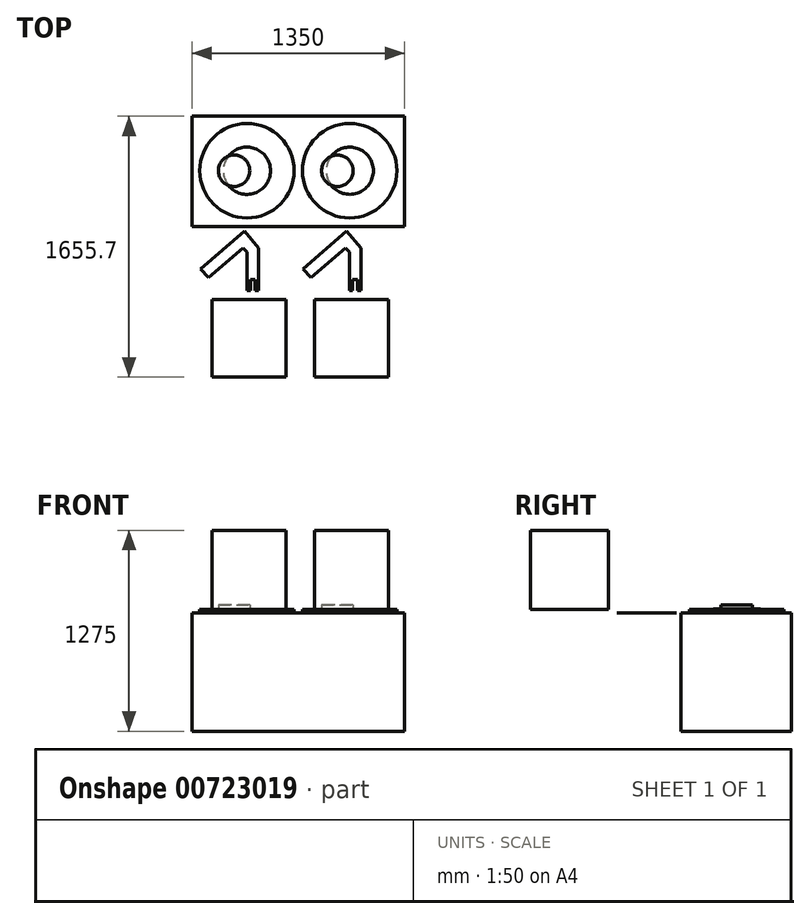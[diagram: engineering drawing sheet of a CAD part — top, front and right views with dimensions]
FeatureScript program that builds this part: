
annotation { "Feature Type Name" : "Feature", "Feature Type Description" : "" }
export const myFeature = defineFeature(function(context is Context, id is Id, definition is map)
    precondition{}
    {
        {
            var Q0;
            Q0=qCreatedBy(makeId("Top.planeOp"),FACE);
            var sketch = newSketch(context, id + "F0", { "sketchPlane" : qUnion([Q0])});
            skLineSegment(sketch, "E0.bottom", {"start": v(-348.1, 345.76) * mm, "end": v(1001.9, 345.76) * mm});
            skLineSegment(sketch, "E0.top", {"start": v(-348.1, -354.24) * mm, "end": v(1001.9, -354.24) * mm});
            skLineSegment(sketch, "E0.left", {"start": v(-348.1, 345.76) * mm, "end": v(-348.1, -354.24) * mm});
            skLineSegment(sketch, "E0.right", {"start": v(1001.9, 345.76) * mm, "end": v(1001.9, -354.24) * mm});
            skSolve(sketch);
        }
        {
            var Q0;
            Q0=makeQuery(id+"F0.imprint","IMPRINT",FACE,{"disambiguationData":[TD([[makeQuery(id+"F0.imprint","IMPRINT",EDGE,{"derivedFrom":sQuery(id+"F0.wireOp",EDGE,"E0.bottom")}),-1.0]])]});
            extrude(context, id + "F1", {"entities" : qUnion([Q0]), "depth" : 750 * mm, "offsetDistance" : 25 * mm});
        }
        {
            var Q0;
            Q0=makeQuery(id+"F1.opExtrude","CAP_FACE",FACE,{"disambiguationData":[OSD([sQuery(id+"F0.wireOp",EDGE,"E0.bottom"),sQuery(id+"F0.wireOp",EDGE,"E0.top"),sQuery(id+"F0.wireOp",EDGE,"E0.left"),sQuery(id+"F0.wireOp",EDGE,"E0.right")])],"isStart":false});
            var sketch = newSketch(context, id + "F2", { "sketchPlane" : qUnion([Q0])});
            skCircle(sketch, "E1", {"center": v(0, 0) * mm, "radius": 300 * mm});
            skCircle(sketch, "E2", {"center": v(652.85, 0) * mm, "radius": 300 * mm});
            skSolve(sketch);
        }
        {
            var Q0;
            Q0=makeQuery(id+"F2.imprint","IMPRINT",FACE,{"disambiguationData":[TD([[makeQuery(id+"F2.imprint","IMPRINT",EDGE,{"derivedFrom":sQuery(id+"F2.wireOp",EDGE,"E1")}),1.0]])]});
            var Q1;
            Q1=makeQuery(id+"F2.imprint","IMPRINT",FACE,{"disambiguationData":[TD([[makeQuery(id+"F2.imprint","IMPRINT",EDGE,{"derivedFrom":sQuery(id+"F2.wireOp",EDGE,"E2")}),1.0]])]});
            extrude(context, id + "F3", {"entities" : qUnion([Q0, Q1]), "operationType" : NewBodyOperationType.ADD, "depth" : 25 * mm, "offsetDistance" : 25 * mm});
        }
        {
            var Q0;
            Q0=makeQuery(id+"F3.opExtrude","CAP_FACE",FACE,{"disambiguationData":[OSD([sQuery(id+"F2.wireOp",EDGE,"E1")])],"isStart":false});
            var sketch = newSketch(context, id + "F4", { "sketchPlane" : qUnion([Q0])});
            skCircle(sketch, "E3", {"center": v(0, 0) * mm, "radius": 150 * mm});
            skCircle(sketch, "E4", {"center": v(652.98, 0) * mm, "radius": 150 * mm});
            skSolve(sketch);
        }
        {
            var Q0;
            Q0=makeQuery(id+"F4.imprint","IMPRINT",FACE,{"disambiguationData":[TD([[makeQuery(id+"F4.imprint","IMPRINT",EDGE,{"derivedFrom":sQuery(id+"F4.wireOp",EDGE,"E3")}),1.0]])]});
            var Q1;
            Q1=makeQuery(id+"F4.imprint","IMPRINT",FACE,{"disambiguationData":[TD([[makeQuery(id+"F4.imprint","IMPRINT",EDGE,{"derivedFrom":sQuery(id+"F4.wireOp",EDGE,"E4")}),1.0]])]});
            extrude(context, id + "F5", {"entities" : qUnion([Q0, Q1]), "operationType" : NewBodyOperationType.ADD, "depth" : 2 * mm, "offsetDistance" : 25 * mm});
        }
        {
            var Q0;
            Q0=makeQuery(id+"F5.opExtrude","CAP_FACE",FACE,{"disambiguationData":[OSD([sQuery(id+"F4.wireOp",EDGE,"E3")])],"isStart":false});
            var sketch = newSketch(context, id + "F6", { "sketchPlane" : qUnion([Q0])});
            skCircle(sketch, "E5", {"center": v(-81.59, 0) * mm, "radius": 100 * mm});
            skCircle(sketch, "E6", {"center": v(574.27, 0) * mm, "radius": 100 * mm});
            skSolve(sketch);
        }
        {
            var Q0;
            {var subQ0=sQuery(id+"F6.wireOp",EDGE,"E5");var subQ1=makeQuery(id+"F5.opExtrude","CAP_EDGE",EDGE,{"disambiguationData":[OSD([sQuery(id+"F4.wireOp",EDGE,"E3")])],"isStart":false});var subQ2=makeQuery(id+"F6.imprint","INTERSECT",VERTEX,{"disambiguationData":[OD(0.0)],"derivedFrom":[subQ1,subQ0]});Q0=makeQuery(id+"F6.imprint","IMPRINT",FACE,{"disambiguationData":[TD([[makeQuery(id+"F6.imprint","IMPRINT",EDGE,{"disambiguationData":[TD([[subQ2,1.0]])],"derivedFrom":subQ0}),1.0]])]});}
            var Q1;
            {var subQ0=sQuery(id+"F6.wireOp",EDGE,"E5");var subQ1=makeQuery(id+"F5.opExtrude","CAP_EDGE",EDGE,{"disambiguationData":[OSD([sQuery(id+"F4.wireOp",EDGE,"E3")])],"isStart":false});var subQ2=makeQuery(id+"F6.imprint","INTERSECT",VERTEX,{"disambiguationData":[OD(0.0)],"derivedFrom":[subQ1,subQ0]});Q1=makeQuery(id+"F6.imprint","IMPRINT",FACE,{"disambiguationData":[TD([[makeQuery(id+"F6.imprint","IMPRINT",EDGE,{"disambiguationData":[TD([[subQ2,-1.0]])],"derivedFrom":subQ0}),1.0]])]});}
            var Q2;
            Q2=makeQuery(id+"F6.imprint","IMPRINT",FACE,{"disambiguationData":[TD([[makeQuery(id+"F6.imprint","IMPRINT",EDGE,{"derivedFrom":sQuery(id+"F6.wireOp",EDGE,"E6")}),1.0]])]});
            extrude(context, id + "F7", {"entities" : qUnion([Q0, Q1, Q2]), "operationType" : NewBodyOperationType.ADD, "depth" : 25 * mm, "offsetDistance" : 25 * mm});
        }
        {
            var Q0;
            Q0=makeQuery(id+"F1.opExtrude","SWEPT_BODY",BODY,{"disambiguationData":[OSD([sQuery(id+"F0.wireOp",EDGE,"E0.bottom"),sQuery(id+"F0.wireOp",EDGE,"E0.top"),sQuery(id+"F0.wireOp",EDGE,"E0.left"),sQuery(id+"F0.wireOp",EDGE,"E0.right")])]});
            transform(context, id + "F8", {"entities" : qUnion([Q0]), "transformType" : TransformType.TRANSLATION_3D, "dx" : 1000 * mm, "dy" : 0 * mm, "dz" : 0 * mm, "makeCopy" : true});
        }
        {
            var Q0;
            Q0=makeQuery(id+"F3.opExtrude","CAP_FACE",FACE,{"disambiguationData":[OSD([sQuery(id+"F2.wireOp",EDGE,"E1")])],"isStart":false});
            var sketch = newSketch(context, id + "F9", { "sketchPlane" : qUnion([Q0])});
            skLineSegment(sketch, "E7.bottom", {"start": v(-221.47, -816.94) * mm, "end": v(248.53, -816.94) * mm});
            skLineSegment(sketch, "E7.top", {"start": v(-221.47, -1309.94) * mm, "end": v(248.53, -1309.94) * mm});
            skLineSegment(sketch, "E7.left", {"start": v(-221.47, -816.94) * mm, "end": v(-221.47, -1309.94) * mm});
            skLineSegment(sketch, "E7.right", {"start": v(248.53, -816.94) * mm, "end": v(248.53, -1309.94) * mm});
            skSolve(sketch);
        }
        {
            var Q0;
            Q0=makeQuery(id+"F9.imprint","IMPRINT",FACE,{"disambiguationData":[TD([[makeQuery(id+"F9.imprint","IMPRINT",EDGE,{"derivedFrom":sQuery(id+"F9.wireOp",EDGE,"E7.bottom")}),-1.0]])]});
            extrude(context, id + "F10", {"entities" : qUnion([Q0]), "depth" : 500 * mm, "offsetDistance" : 25 * mm});
        }
        {
            var Q0;
            Q0=makeQuery(id+"F1.opExtrude","CAP_FACE",FACE,{"disambiguationData":[OSD([sQuery(id+"F0.wireOp",EDGE,"E0.bottom"),sQuery(id+"F0.wireOp",EDGE,"E0.top"),sQuery(id+"F0.wireOp",EDGE,"E0.left"),sQuery(id+"F0.wireOp",EDGE,"E0.right")])],"isStart":false});
            var sketch = newSketch(context, id + "F11", { "sketchPlane" : qUnion([Q0])});
            skLineSegment(sketch, "E8", {"start": v(-293.8, -623.4) * mm, "end": v(-16.38, -383.6) * mm});
            skLineSegment(sketch, "E9", {"start": v(-16.38, -383.6) * mm, "end": v(75.4, -489.78) * mm});
            skLineSegment(sketch, "E10", {"start": v(75.4, -489.78) * mm, "end": v(75.4, -760.85) * mm});
            skLineSegment(sketch, "E11", {"start": v(75.4, -760.85) * mm, "end": v(52.32, -760.85) * mm});
            skLineSegment(sketch, "E12", {"start": v(0, -760.85) * mm, "end": v(0, -517.45) * mm});
            skLineSegment(sketch, "E13", {"start": v(-243.5, -677.84) * mm, "end": v(-293.8, -623.4) * mm});
            skLineSegment(sketch, "E14", {"start": v(-243.5, -677.84) * mm, "end": v(-23.94, -489.54) * mm});
            skLineSegment(sketch, "E15", {"start": v(-23.94, -489.54) * mm, "end": v(0, -517.45) * mm});
            skLineSegment(sketch, "E16", {"start": v(21.8, -760.85) * mm, "end": v(21.8, -690.16) * mm});
            skLineSegment(sketch, "E17", {"start": v(21.8, -690.16) * mm, "end": v(52.32, -690.16) * mm});
            skLineSegment(sketch, "E18", {"start": v(52.32, -690.16) * mm, "end": v(52.32, -760.85) * mm});
            skLineSegment(sketch, "E19.trimOffspring", {"start": v(21.8, -760.85) * mm, "end": v(0, -760.85) * mm});
            skSolve(sketch);
        }
        {
            var Q0;
            Q0=makeQuery(id+"F11.imprint","IMPRINT",FACE,{"disambiguationData":[TD([[makeQuery(id+"F11.imprint","IMPRINT",EDGE,{"derivedFrom":sQuery(id+"F11.wireOp",EDGE,"E8")}),-1.0]])]});
            extrude(context, id + "F12", {"entities" : qUnion([Q0]), "depth" : 2 * mm, "offsetDistance" : 25 * mm});
        }
        {
            var Q0;
            Q0=makeQuery(id+"F10.opExtrude","SWEPT_BODY",BODY,{"disambiguationData":[OSD([sQuery(id+"F9.wireOp",EDGE,"E7.bottom"),sQuery(id+"F9.wireOp",EDGE,"E7.top"),sQuery(id+"F9.wireOp",EDGE,"E7.left"),sQuery(id+"F9.wireOp",EDGE,"E7.right")])]});
            transform(context, id + "F13", {"entities" : qUnion([Q0]), "transformType" : TransformType.TRANSLATION_3D, "dx" : 1000 * mm, "dy" : 0 * mm, "dz" : 0 * mm, "makeCopy" : true});
        }
        {
            var Q0;
            Q0=makeQuery(id+"F12.opExtrude","SWEPT_BODY",BODY,{"disambiguationData":[OSD([sQuery(id+"F11.wireOp",EDGE,"E8"),sQuery(id+"F11.wireOp",EDGE,"E9"),sQuery(id+"F11.wireOp",EDGE,"E10"),sQuery(id+"F11.wireOp",EDGE,"E11"),sQuery(id+"F11.wireOp",EDGE,"E12"),sQuery(id+"F11.wireOp",EDGE,"E13"),sQuery(id+"F11.wireOp",EDGE,"E14"),sQuery(id+"F11.wireOp",EDGE,"E15"),sQuery(id+"F11.wireOp",EDGE,"E16"),sQuery(id+"F11.wireOp",EDGE,"E17"),sQuery(id+"F11.wireOp",EDGE,"E18"),sQuery(id+"F11.wireOp",EDGE,"E19.trimOffspring")])]});
            transform(context, id + "F14", {"entities" : qUnion([Q0]), "transformType" : TransformType.TRANSLATION_3D, "dx" : 1000 * mm, "dy" : 0 * mm, "dz" : 0 * mm, "makeCopy" : true});
        }
        {
            var Q0;
            Q0=makeQuery(id+"F8.opPattern","COPY",BODY,{"derivedFrom":makeQuery(id+"F1.opExtrude","SWEPT_BODY",BODY,{"disambiguationData":[OSD([sQuery(id+"F0.wireOp",EDGE,"E0.bottom"),sQuery(id+"F0.wireOp",EDGE,"E0.top"),sQuery(id+"F0.wireOp",EDGE,"E0.left"),sQuery(id+"F0.wireOp",EDGE,"E0.right")])]}),"instanceName":"1"});
            deleteBodies(context, id + "F15", {"entities" : qUnion([Q0])});
        }
        {
            var Q0;
            Q0=makeQuery(id+"F14.opPattern","COPY",BODY,{"derivedFrom":makeQuery(id+"F12.opExtrude","SWEPT_BODY",BODY,{"disambiguationData":[OSD([sQuery(id+"F11.wireOp",EDGE,"E8"),sQuery(id+"F11.wireOp",EDGE,"E9"),sQuery(id+"F11.wireOp",EDGE,"E10"),sQuery(id+"F11.wireOp",EDGE,"E11"),sQuery(id+"F11.wireOp",EDGE,"E12"),sQuery(id+"F11.wireOp",EDGE,"E13"),sQuery(id+"F11.wireOp",EDGE,"E14"),sQuery(id+"F11.wireOp",EDGE,"E15"),sQuery(id+"F11.wireOp",EDGE,"E16"),sQuery(id+"F11.wireOp",EDGE,"E17"),sQuery(id+"F11.wireOp",EDGE,"E18"),sQuery(id+"F11.wireOp",EDGE,"E19.trimOffspring")])]}),"instanceName":"1"});
            var Q1;
            Q1=makeQuery(id+"F13.opPattern","COPY",BODY,{"derivedFrom":makeQuery(id+"F10.opExtrude","SWEPT_BODY",BODY,{"disambiguationData":[OSD([sQuery(id+"F9.wireOp",EDGE,"E7.bottom"),sQuery(id+"F9.wireOp",EDGE,"E7.top"),sQuery(id+"F9.wireOp",EDGE,"E7.left"),sQuery(id+"F9.wireOp",EDGE,"E7.right")])]}),"instanceName":"1"});
            deleteBodies(context, id + "F16", {"entities" : qUnion([Q0, Q1])});
        }
        {
            var Q0;
            Q0=makeQuery(id+"F10.opExtrude","SWEPT_BODY",BODY,{"disambiguationData":[OSD([sQuery(id+"F9.wireOp",EDGE,"E7.bottom"),sQuery(id+"F9.wireOp",EDGE,"E7.top"),sQuery(id+"F9.wireOp",EDGE,"E7.left"),sQuery(id+"F9.wireOp",EDGE,"E7.right")])]});
            transform(context, id + "F17", {"entities" : qUnion([Q0]), "transformType" : TransformType.TRANSLATION_3D, "dx" : 650 * mm, "dy" : 0 * mm, "dz" : 0 * mm, "makeCopy" : true});
        }
        {
            var Q0;
            Q0=makeQuery(id+"F12.opExtrude","SWEPT_BODY",BODY,{"disambiguationData":[OSD([sQuery(id+"F11.wireOp",EDGE,"E8"),sQuery(id+"F11.wireOp",EDGE,"E9"),sQuery(id+"F11.wireOp",EDGE,"E10"),sQuery(id+"F11.wireOp",EDGE,"E11"),sQuery(id+"F11.wireOp",EDGE,"E12"),sQuery(id+"F11.wireOp",EDGE,"E13"),sQuery(id+"F11.wireOp",EDGE,"E14"),sQuery(id+"F11.wireOp",EDGE,"E15"),sQuery(id+"F11.wireOp",EDGE,"E16"),sQuery(id+"F11.wireOp",EDGE,"E17"),sQuery(id+"F11.wireOp",EDGE,"E18"),sQuery(id+"F11.wireOp",EDGE,"E19.trimOffspring")])]});
            transform(context, id + "F18", {"entities" : qUnion([Q0]), "transformType" : TransformType.TRANSLATION_3D, "dx" : 650 * mm, "dy" : 0 * mm, "dz" : 0 * mm, "makeCopy" : true});
        }
    });
